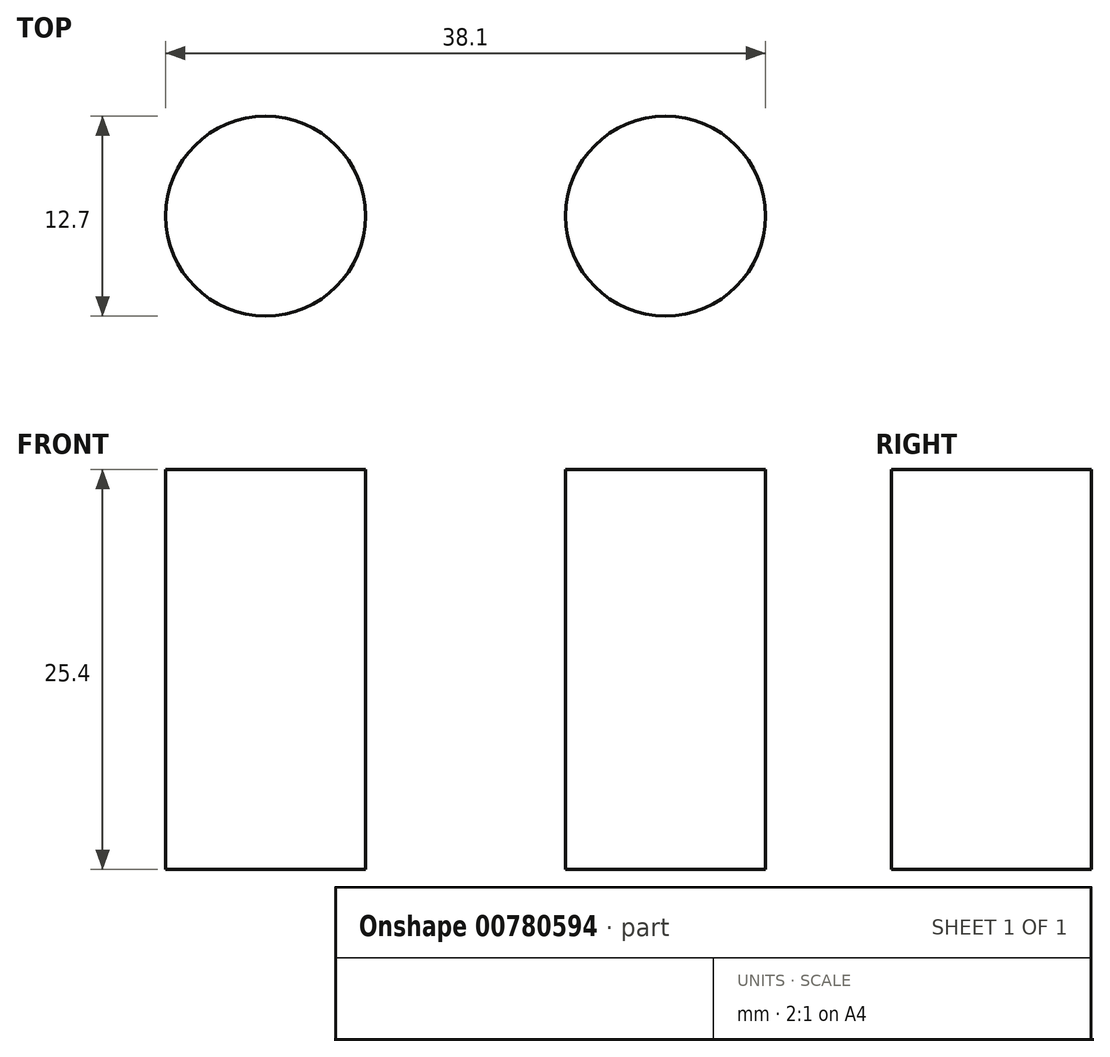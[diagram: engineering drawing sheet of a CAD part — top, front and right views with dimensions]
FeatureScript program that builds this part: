
annotation { "Feature Type Name" : "Feature", "Feature Type Description" : "" }
export const myFeature = defineFeature(function(context is Context, id is Id, definition is map)
    precondition{}
    {
        {
            var Q0;
            Q0=qCreatedBy(makeId("Top.planeOp"),FACE);
            var sketch = newSketch(context, id + "F0", { "sketchPlane" : qUnion([Q0])});
            skCircle(sketch, "E0", {"center": v(0, 0) * mm, "radius": 6.35 * mm});
            skCircle(sketch, "E1", {"center": v(-25.4, 0) * mm, "radius": 6.35 * mm});
            skSolve(sketch);
        }
        {
            var Q0;
            Q0 = qSketchRegion(id + "F0", true);
            extrude(context, id + "F1", {"entities" : qUnion([Q0]), "depth" : 25.4 * mm, "offsetDistance" : 25.4 * mm});
        }
    });
